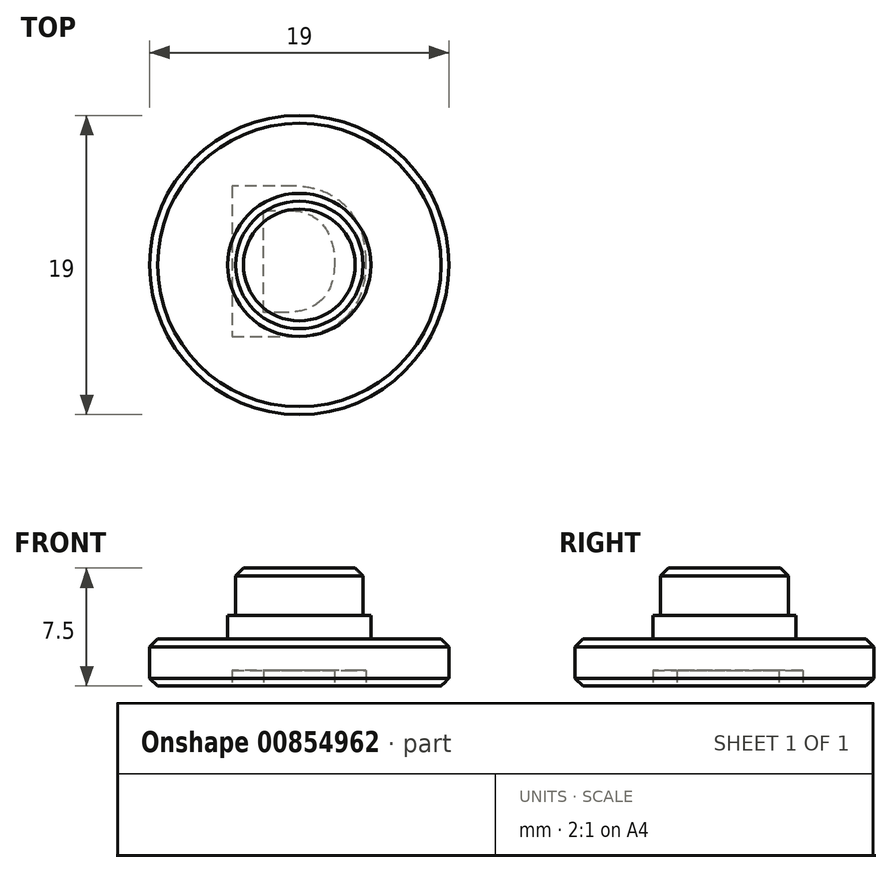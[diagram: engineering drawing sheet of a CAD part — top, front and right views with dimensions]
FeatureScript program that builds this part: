
annotation { "Feature Type Name" : "Feature", "Feature Type Description" : "" }
export const myFeature = defineFeature(function(context is Context, id is Id, definition is map)
    precondition{}
    {
        {
            var Q0;
            Q0=qCreatedBy(makeId("Top.planeOp"),FACE);
            var sketch = newSketch(context, id + "F0", { "sketchPlane" : qUnion([Q0])});
            skCircle(sketch, "E0", {"center": v(0, 0) * mm, "radius": 9.5 * mm});
            skSolve(sketch);
        }
        {
            var Q0;
            Q0=qSketchRegion(id+"F0",true);
            extrude(context, id + "F1", {"entities" : qUnion([Q0]), "depth" : 3 * mm, "offsetDistance" : 25 * mm});
        }
        {
            var Q0;
            Q0=makeQuery(id+"F1.opExtrude","CAP_FACE",FACE,{"disambiguationData":[OSD([sQuery(id+"F0.wireOp",EDGE,"E0")])],"isStart":false});
            var sketch = newSketch(context, id + "F2", { "sketchPlane" : qUnion([Q0])});
            skCircle(sketch, "E1", {"center": v(0, 0) * mm, "radius": 4.05 * mm});
            skSolve(sketch);
        }
        {
            var Q0;
            Q0=qSketchRegion(id+"F2",true);
            extrude(context, id + "F3", {"entities" : qUnion([Q0]), "operationType" : NewBodyOperationType.ADD, "depth" : 4.5 * mm, "offsetDistance" : 25 * mm});
        }
        {
            var Q0;
            Q0=makeQuery(id+"F3.opExtrude","CAP_EDGE",EDGE,{"disambiguationData":[OSD([sQuery(id+"F2.wireOp",EDGE,"E1")])],"isStart":false});
            var Q1;
            Q1=makeQuery(id+"F1.opExtrude","CAP_EDGE",EDGE,{"disambiguationData":[OSD([sQuery(id+"F0.wireOp",EDGE,"E0")])],"isStart":false});
            var Q2;
            Q2=makeQuery(id+"F1.opExtrude","CAP_EDGE",EDGE,{"disambiguationData":[OSD([sQuery(id+"F0.wireOp",EDGE,"E0")])],"isStart":true});
            chamfer(context, id + "F4", {"entities" : qUnion([Q0, Q1, Q2]), "width" : 0.5 * mm, "tangentPropagation" : true});
        }
        {
            var Q0;
            Q0=makeQuery(id+"F1.opExtrude","CAP_FACE",FACE,{"disambiguationData":[OSD([sQuery(id+"F0.wireOp",EDGE,"E0")])],"isStart":false});
            var sketch = newSketch(context, id + "F5", { "sketchPlane" : qUnion([Q0])});
            skCircle(sketch, "E2", {"center": v(0, 0) * mm, "radius": 4.55 * mm});
            skSolve(sketch);
        }
        {
            var Q0;
            Q0=qSketchRegion(id+"F5",true);
            extrude(context, id + "F6", {"entities" : qUnion([Q0]), "operationType" : NewBodyOperationType.ADD, "depth" : 1.5 * mm, "offsetDistance" : 25 * mm});
        }
        {
            var Q0;
            Q0=makeQuery(id+"F1.opExtrude","CAP_FACE",FACE,{"disambiguationData":[OSD([sQuery(id+"F0.wireOp",EDGE,"E0")])],"isStart":true});
            var sketch = newSketch(context, id + "F7", { "sketchPlane" : qUnion([Q0])});
            skText(sketch, "E3", { "text": "D", "fontName": "Arimo-Bold.ttf"});
            const initialGuessF7  = {"E3": [-0.0052, -0.005, 1, 0, 0.01]};
            skSetInitialGuess(sketch, initialGuessF7);
            skSolve(sketch);
        }
        {
            var Q0;
            Q0 = qSketchRegion(id + "F7", true);
            extrude(context, id + "F8", {"entities" : qUnion([Q0]), "operationType" : NewBodyOperationType.REMOVE, "oppositeDirection" : true, "depth" : 1 * mm, "offsetDistance" : 25 * mm});
        }
    });
